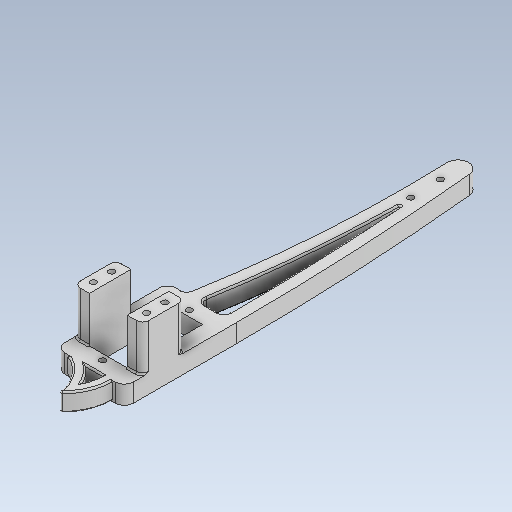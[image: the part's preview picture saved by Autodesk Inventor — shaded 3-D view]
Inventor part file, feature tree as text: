
AUTODESK INVENTOR PART (.ipt)
format: ipt  version: 2020.3 (Build 243373000, 373)  size: 272,384 bytes
history: native  units: mm
features: other x3, sketch x2
ambient origin geometry x8: Origin, YZ Plane, XZ Plane, XY Plane, X Axis, Y Axis, Z Axis, Center Point
bodies: Solid1 (feature_tree)
feature tree (5):
  other  "LegEnd_Right_v1.ipt"
  other  "Solid1::LegEnd_Right_v1.ipt"
  other  "TaggingFeature1"
  sketch  "Sketch1"  dims[d0=10.0mm]
  sketch  "Sketch3"
